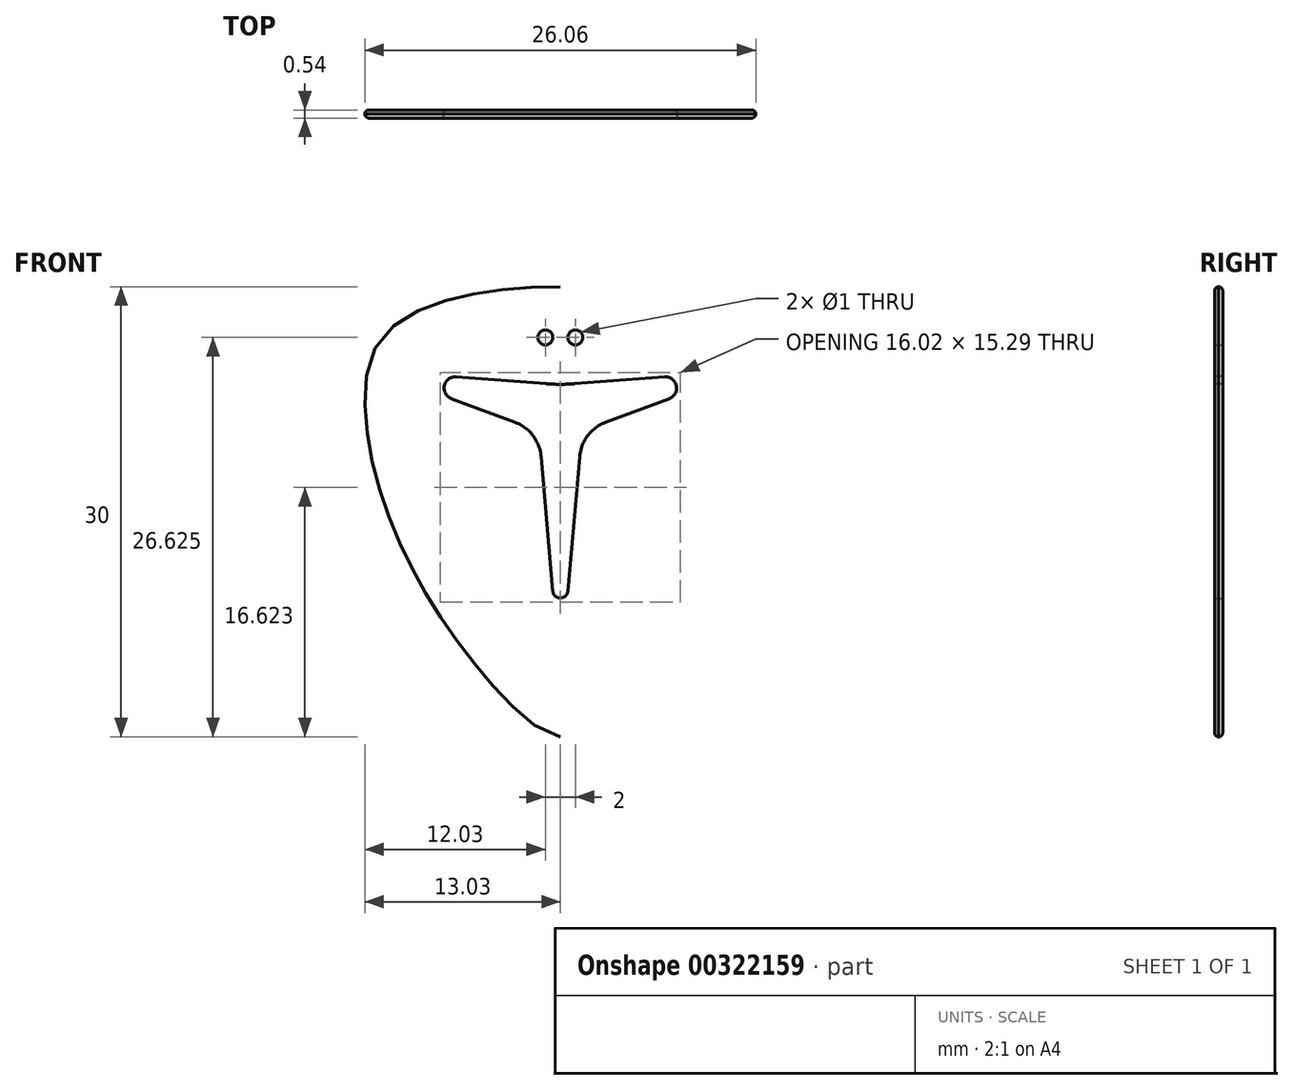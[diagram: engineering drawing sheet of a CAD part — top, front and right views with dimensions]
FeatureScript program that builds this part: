
annotation { "Feature Type Name" : "Feature", "Feature Type Description" : "" }
export const myFeature = defineFeature(function(context is Context, id is Id, definition is map)
    precondition{}
    {
        {
            var Q0;
            Q0=qCreatedBy(makeId("Front.planeOp"),FACE);
            var sketch = newSketch(context, id + "F0", { "sketchPlane" : qUnion([Q0])});
            skLineSegment(sketch, "E0", {"start": v(0, 0) * mm, "end": v(0, 6.75) * mm, "construction": true});
            skLineSegment(sketch, "E1", {"start": v(0, 0) * mm, "end": v(0, -23.25) * mm, "construction": true});
            skLineSegment(sketch, "E2", {"start": v(0, 0) * mm, "end": v(13, 0) * mm, "construction": true});
            skFitSpline(sketch, "E3", {"points": [v(0, -23.25) * mm, v(9.5, -12.75) * mm, v(13, 0) * mm, v(11, 4.25) * mm, v(0, 6.75) * mm], "startDerivative": vector(20.6, 0) * mm, "endDerivative": vector(-57.72, 0) * mm});
            skFitSpline(sketch, "E4.MirrorCS", {"points": [v(0, -23.25) * mm, v(-9.5, -12.75) * mm, v(-13, 0) * mm, v(-11, 4.25) * mm, v(0, 6.75) * mm], "startDerivative": vector(-20.6, 0) * mm, "endDerivative": vector(57.72, 0) * mm});
            skArc(sketch, "E5", {"start": v(7.26, -0.7) * mm, "mid": v(7.73, 0.16) * mm, "end": v(6.94, 0.75) * mm});
            skLineSegment(sketch, "E6", {"start": v(7.26, -0.7) * mm, "end": v(3.04, -2.27) * mm});
            skArc(sketch, "E7", {"start": v(3.04, -2.27) * mm, "mid": v(1.83, -3.17) * mm, "end": v(1.28, -4.58) * mm});
            skLineSegment(sketch, "E8", {"start": v(0.5, -13.54) * mm, "end": v(1.28, -4.58) * mm});
            skArc(sketch, "E9", {"start": v(0, -14) * mm, "mid": v(0.34, -13.87) * mm, "end": v(0.5, -13.54) * mm});
            skArc(sketch, "E10.MirrorCS", {"start": v(0, -14) * mm, "mid": v(-0.34, -13.87) * mm, "end": v(-0.5, -13.54) * mm});
            skLineSegment(sketch, "E11.MirrorCS", {"start": v(-0.5, -13.54) * mm, "end": v(-1.28, -4.58) * mm});
            skArc(sketch, "E12.MirrorCS", {"start": v(-3.04, -2.27) * mm, "mid": v(-1.83, -3.17) * mm, "end": v(-1.28, -4.58) * mm});
            skLineSegment(sketch, "E13.MirrorCS", {"start": v(-7.26, -0.7) * mm, "end": v(-3.04, -2.27) * mm});
            skArc(sketch, "E14.MirrorCS", {"start": v(-7.26, -0.7) * mm, "mid": v(-7.73, 0.16) * mm, "end": v(-6.94, 0.75) * mm});
            skLineSegment(sketch, "E15", {"start": v(6.94, 0.75) * mm, "end": v(0.96, 0.29) * mm});
            skArc(sketch, "E16", {"start": v(0, 0.25) * mm, "mid": v(0.48, 0.26) * mm, "end": v(0.96, 0.29) * mm});
            skArc(sketch, "E17.MirrorCS", {"start": v(0, 0.25) * mm, "mid": v(-0.48, 0.26) * mm, "end": v(-0.96, 0.29) * mm});
            skLineSegment(sketch, "E18.MirrorCS", {"start": v(-6.94, 0.75) * mm, "end": v(-0.96, 0.29) * mm});
            skLineSegment(sketch, "E19", {"start": v(0, 3.38) * mm, "end": v(1, 3.38) * mm});
            skCircle(sketch, "E20", {"center": v(1, 3.38) * mm, "radius": 0.5 * mm});
            skLineSegment(sketch, "E21.MirrorCS", {"start": v(0, 3.38) * mm, "end": v(-1, 3.38) * mm});
            skCircle(sketch, "E22.MirrorC", {"center": v(-1, 3.38) * mm, "radius": 0.5 * mm});
            skSolve(sketch);
        }
        {
            var Q0;
            Q0=qSketchRegion(id+"F0",true);
            extrude(context, id + "F1", {"entities" : qUnion([Q0]), "depth" : 0.54 * mm});
        }
        {
            var Q0;
            Q0=makeQuery(id+"F1.opExtrude","CAP_EDGE",EDGE,{"disambiguationData":[OSD([sQuery(id+"F0.wireOp",EDGE,"E5")])],"isStart":false});
            var Q1;
            Q1=makeQuery(id+"F1.opExtrude","CAP_EDGE",EDGE,{"disambiguationData":[OSD([sQuery(id+"F0.wireOp",EDGE,"E7")])],"isStart":true});
            var Q2;
            Q2=makeQuery(id+"F1.opExtrude","CAP_EDGE",EDGE,{"disambiguationData":[OSD([sQuery(id+"F0.wireOp",EDGE,"E14.MirrorCS")])],"isStart":false});
            var Q3;
            Q3=makeQuery(id+"F1.opExtrude","CAP_EDGE",EDGE,{"disambiguationData":[OSD([sQuery(id+"F0.wireOp",EDGE,"E5")])],"isStart":true});
            var Q4;
            Q4=makeQuery(id+"F1.opExtrude","CAP_EDGE",EDGE,{"disambiguationData":[OSD([sQuery(id+"F0.wireOp",EDGE,"E12.MirrorCS")])],"isStart":false});
            var Q5;
            Q5=makeQuery(id+"F1.opExtrude","CAP_EDGE",EDGE,{"disambiguationData":[OSD([sQuery(id+"F0.wireOp",EDGE,"E7")])],"isStart":false});
            var Q6;
            Q6=makeQuery(id+"F1.opExtrude","CAP_EDGE",EDGE,{"disambiguationData":[OSD([sQuery(id+"F0.wireOp",EDGE,"cP70XH3B-hxny-nh1n-TbyW-52Zl4TOD4HrO"),sQuery(id+"F0.wireOp",EDGE,"9cf6c757-e815-40dd-95a7-672993b90d513.MirrorCS")])],"isStart":true});
            var Q7;
            Q7=makeQuery(id+"F1.opExtrude","CAP_EDGE",EDGE,{"disambiguationData":[OSD([sQuery(id+"F0.wireOp",EDGE,"E13.MirrorCS")])],"isStart":false});
            var Q8;
            Q8=makeQuery(id+"F1.opExtrude","CAP_EDGE",EDGE,{"disambiguationData":[OSD([sQuery(id+"F0.wireOp",EDGE,"E12.MirrorCS")])],"isStart":true});
            var Q9;
            Q9=makeQuery(id+"F1.opExtrude","CAP_EDGE",EDGE,{"disambiguationData":[OSD([sQuery(id+"F0.wireOp",EDGE,"cP70XH3B-hxny-nh1n-TbyW-52Zl4TOD4HrO"),sQuery(id+"F0.wireOp",EDGE,"9cf6c757-e815-40dd-95a7-672993b90d513.MirrorCS")])],"isStart":false});
            var Q10;
            Q10=makeQuery(id+"F1.opExtrude","CAP_EDGE",EDGE,{"disambiguationData":[OSD([sQuery(id+"F0.wireOp",EDGE,"E9"),sQuery(id+"F0.wireOp",EDGE,"E10.MirrorCS")])],"isStart":true});
            var Q11;
            Q11=makeQuery(id+"F1.opExtrude","SWEPT_EDGE",EDGE,{"disambiguationData":[OSD([sQuery(id+"F0.wireOp",EDGE,"9cf6c757-e815-40dd-95a7-672993b90d513.MirrorCS"),sQuery(id+"F0.wireOp",EDGE,"E14.MirrorCS")])]});
            var Q12;
            Q12=makeQuery(id+"F1.opExtrude","CAP_EDGE",EDGE,{"disambiguationData":[OSD([sQuery(id+"F0.wireOp",EDGE,"E8")])],"isStart":true});
            var Q13;
            Q13=makeQuery(id+"F1.opExtrude","CAP_EDGE",EDGE,{"disambiguationData":[OSD([sQuery(id+"F0.wireOp",EDGE,"E11.MirrorCS")])],"isStart":false});
            var Q14;
            Q14=makeQuery(id+"F1.opExtrude","SWEPT_EDGE",EDGE,{"disambiguationData":[OSD([sQuery(id+"F0.wireOp",EDGE,"E6"),sQuery(id+"F0.wireOp",EDGE,"E7")])]});
            var Q15;
            Q15=makeQuery(id+"F1.opExtrude","SWEPT_EDGE",EDGE,{"disambiguationData":[OSD([sQuery(id+"F0.wireOp",EDGE,"E8"),sQuery(id+"F0.wireOp",EDGE,"E9")])]});
            var Q16;
            Q16=makeQuery(id+"F1.opExtrude","SWEPT_EDGE",EDGE,{"disambiguationData":[OSD([sQuery(id+"F0.wireOp",EDGE,"E13.MirrorCS"),sQuery(id+"F0.wireOp",EDGE,"E14.MirrorCS")])]});
            var Q17;
            Q17=makeQuery(id+"F1.opExtrude","SWEPT_EDGE",EDGE,{"disambiguationData":[OSD([sQuery(id+"F0.wireOp",EDGE,"E10.MirrorCS"),sQuery(id+"F0.wireOp",EDGE,"E11.MirrorCS")])]});
            var Q18;
            Q18=makeQuery(id+"F1.opExtrude","SWEPT_EDGE",EDGE,{"disambiguationData":[OSD([sQuery(id+"F0.wireOp",EDGE,"E11.MirrorCS"),sQuery(id+"F0.wireOp",EDGE,"E12.MirrorCS")])]});
            var Q19;
            Q19=makeQuery(id+"F1.opExtrude","SWEPT_EDGE",EDGE,{"disambiguationData":[OSD([sQuery(id+"F0.wireOp",EDGE,"E5"),sQuery(id+"F0.wireOp",EDGE,"E6")])]});
            var Q20;
            Q20=makeQuery(id+"F1.opExtrude","CAP_EDGE",EDGE,{"disambiguationData":[OSD([sQuery(id+"F0.wireOp",EDGE,"E14.MirrorCS")])],"isStart":true});
            var Q21;
            Q21=makeQuery(id+"F1.opExtrude","SWEPT_EDGE",EDGE,{"disambiguationData":[OSD([sQuery(id+"F0.wireOp",EDGE,"E12.MirrorCS"),sQuery(id+"F0.wireOp",EDGE,"E13.MirrorCS")])]});
            var Q22;
            Q22=makeQuery(id+"F1.opExtrude","CAP_EDGE",EDGE,{"disambiguationData":[OSD([sQuery(id+"F0.wireOp",EDGE,"E8")])],"isStart":false});
            var Q23;
            Q23=makeQuery(id+"F1.opExtrude","SWEPT_EDGE",EDGE,{"disambiguationData":[OSD([sQuery(id+"F0.wireOp",EDGE,"cP70XH3B-hxny-nh1n-TbyW-52Zl4TOD4HrO"),sQuery(id+"F0.wireOp",EDGE,"E5")])]});
            var Q24;
            Q24=makeQuery(id+"F1.opExtrude","CAP_EDGE",EDGE,{"disambiguationData":[OSD([sQuery(id+"F0.wireOp",EDGE,"E6")])],"isStart":false});
            var Q25;
            Q25=makeQuery(id+"F1.opExtrude","CAP_EDGE",EDGE,{"disambiguationData":[OSD([sQuery(id+"F0.wireOp",EDGE,"E11.MirrorCS")])],"isStart":true});
            var Q26;
            Q26=makeQuery(id+"F1.opExtrude","SWEPT_EDGE",EDGE,{"disambiguationData":[OSD([sQuery(id+"F0.wireOp",EDGE,"E7"),sQuery(id+"F0.wireOp",EDGE,"E8")])]});
            var Q27;
            Q27=makeQuery(id+"F1.opExtrude","CAP_EDGE",EDGE,{"disambiguationData":[OSD([sQuery(id+"F0.wireOp",EDGE,"E6")])],"isStart":true});
            var Q28;
            Q28=makeQuery(id+"F1.opExtrude","CAP_EDGE",EDGE,{"disambiguationData":[OSD([sQuery(id+"F0.wireOp",EDGE,"E13.MirrorCS")])],"isStart":true});
            var Q29;
            Q29=makeQuery(id+"F1.opExtrude","CAP_EDGE",EDGE,{"disambiguationData":[OSD([sQuery(id+"F0.wireOp",EDGE,"E18.MirrorCS")])],"isStart":false});
            var Q30;
            Q30=makeQuery(id+"F1.opExtrude","CAP_EDGE",EDGE,{"disambiguationData":[OSD([sQuery(id+"F0.wireOp",EDGE,"E18.MirrorCS")])],"isStart":true});
            var Q31;
            Q31=makeQuery(id+"F1.opExtrude","CAP_EDGE",EDGE,{"disambiguationData":[OSD([sQuery(id+"F0.wireOp",EDGE,"E16"),sQuery(id+"F0.wireOp",EDGE,"E17.MirrorCS")])],"isStart":false});
            fillet(context, id + "F2", {"entities" : qUnion([Q0, Q1, Q2, Q3, Q4, Q5, Q6, Q7, Q8, Q9, Q10, Q11, Q12, Q13, Q14, Q15, Q16, Q17, Q18, Q19, Q20, Q21, Q22, Q23, Q24, Q25, Q26, Q27, Q28, Q29, Q30, Q31]), "radius" : (0.54 / 2) * mm, "tangentPropagation" : true, "allowEdgeOverflow" : false});
        }
        {
            var Q0;
            Q0=makeQuery(id+"F1.opExtrude","CAP_EDGE",EDGE,{"disambiguationData":[OSD([sQuery(id+"F0.wireOp",EDGE,"E4.MirrorCS")])],"isStart":false});
            var Q1;
            Q1=makeQuery(id+"F1.opExtrude","CAP_EDGE",EDGE,{"disambiguationData":[OSD([sQuery(id+"F0.wireOp",EDGE,"E3")])],"isStart":false});
            var Q2;
            Q2=makeQuery(id+"F1.opExtrude","CAP_EDGE",EDGE,{"disambiguationData":[OSD([sQuery(id+"F0.wireOp",EDGE,"E4.MirrorCS")])],"isStart":true});
            var Q3;
            Q3=makeQuery(id+"F1.opExtrude","CAP_EDGE",EDGE,{"disambiguationData":[OSD([sQuery(id+"F0.wireOp",EDGE,"E3")])],"isStart":true});
            fillet(context, id + "F3", {"entities" : qUnion([Q0, Q1, Q2, Q3]), "radius" : 0.54 / 2 * mm, "tangentPropagation" : true, "allowEdgeOverflow" : false});
        }
    });
